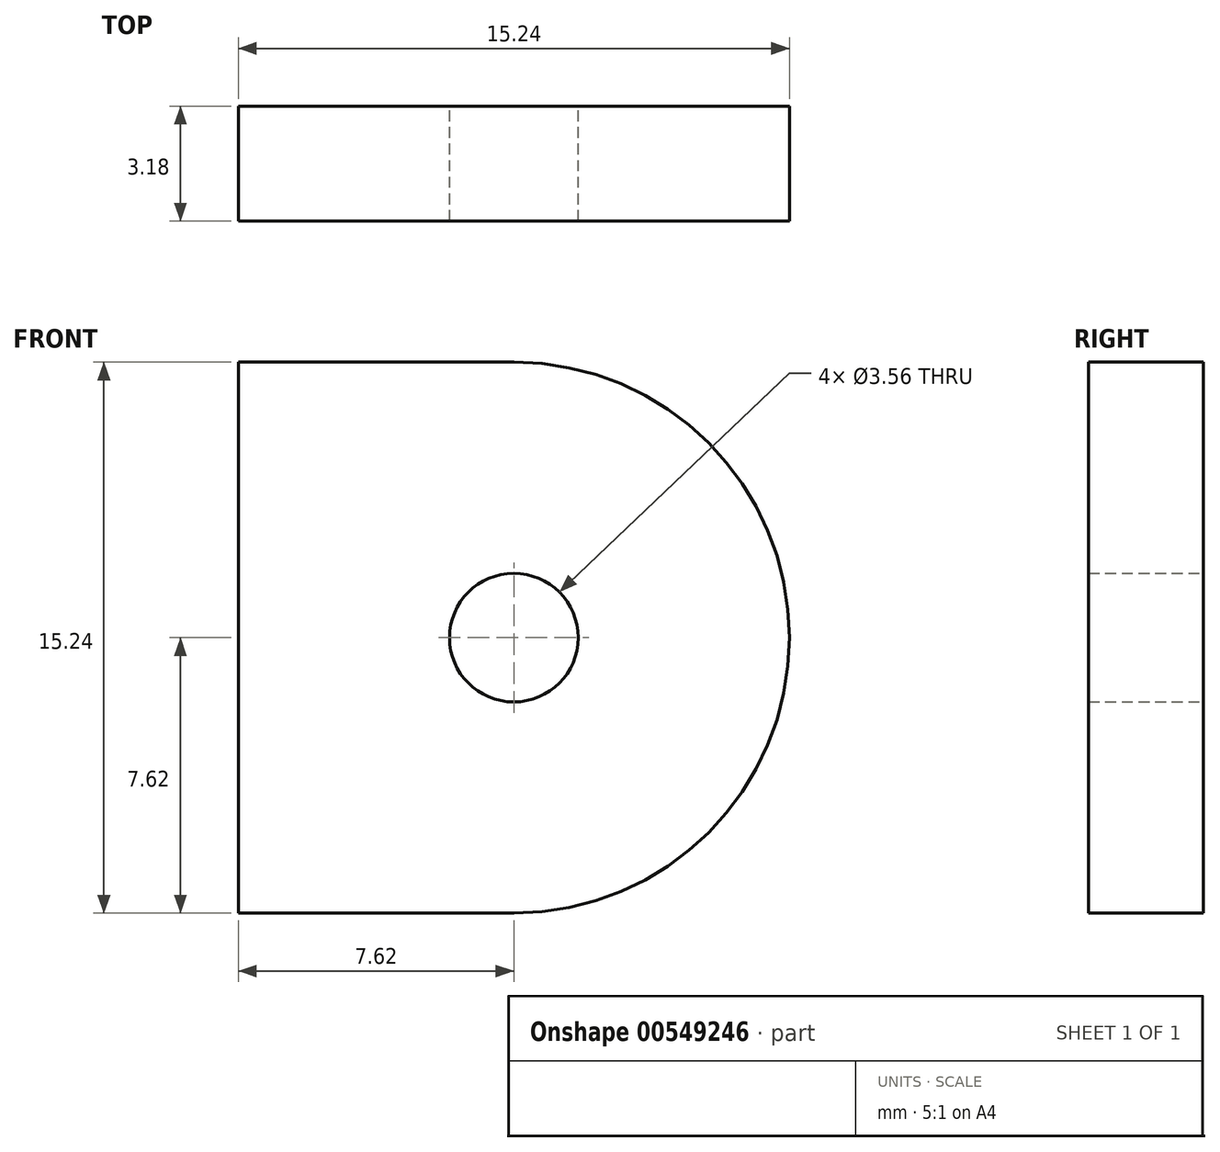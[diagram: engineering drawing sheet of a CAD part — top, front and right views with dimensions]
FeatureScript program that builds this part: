
annotation { "Feature Type Name" : "Feature", "Feature Type Description" : "" }
export const myFeature = defineFeature(function(context is Context, id is Id, definition is map)
    precondition{}
    {
        {
            var Q0;
            Q0=qCreatedBy(makeId("Front.planeOp"),FACE);
            var sketch = newSketch(context, id + "F0", { "sketchPlane" : qUnion([Q0])});
            skPoint(sketch, "E0.middle", {"position": v(0, 0) * mm});
            skCircle(sketch, "E1", {"center": v(19.05, -3.8) * mm, "radius": 1.78 * mm});
            skLineSegment(sketch, "E2", {"start": v(19.05, -3.8) * mm, "end": v(15.42, -3.8) * mm, "construction": true});
            skArc(sketch, "E3", {"start": v(19.05, -11.43) * mm, "mid": v(26.67, -3.8) * mm, "end": v(19.05, 3.81) * mm});
            skLineSegment(sketch, "E4", {"start": v(19.05, 3.81) * mm, "end": v(11.43, 3.81) * mm});
            skLineSegment(sketch, "E5", {"start": v(11.43, 3.81) * mm, "end": v(11.43, -3.8) * mm});
            skLineSegment(sketch, "E6", {"start": v(11.43, -3.8) * mm, "end": v(11.43, -11.43) * mm});
            skLineSegment(sketch, "E7", {"start": v(11.43, -11.43) * mm, "end": v(19.05, -11.43) * mm});
            skSolve(sketch);
        }
        {
            var Q0;
            Q0=qSketchRegion(id+"F0",true);
            extrude(context, id + "F1", {"entities" : qUnion([Q0]), "depth" : 3.17 * mm, "offsetDistance" : 25.4 * mm});
        }
    });
